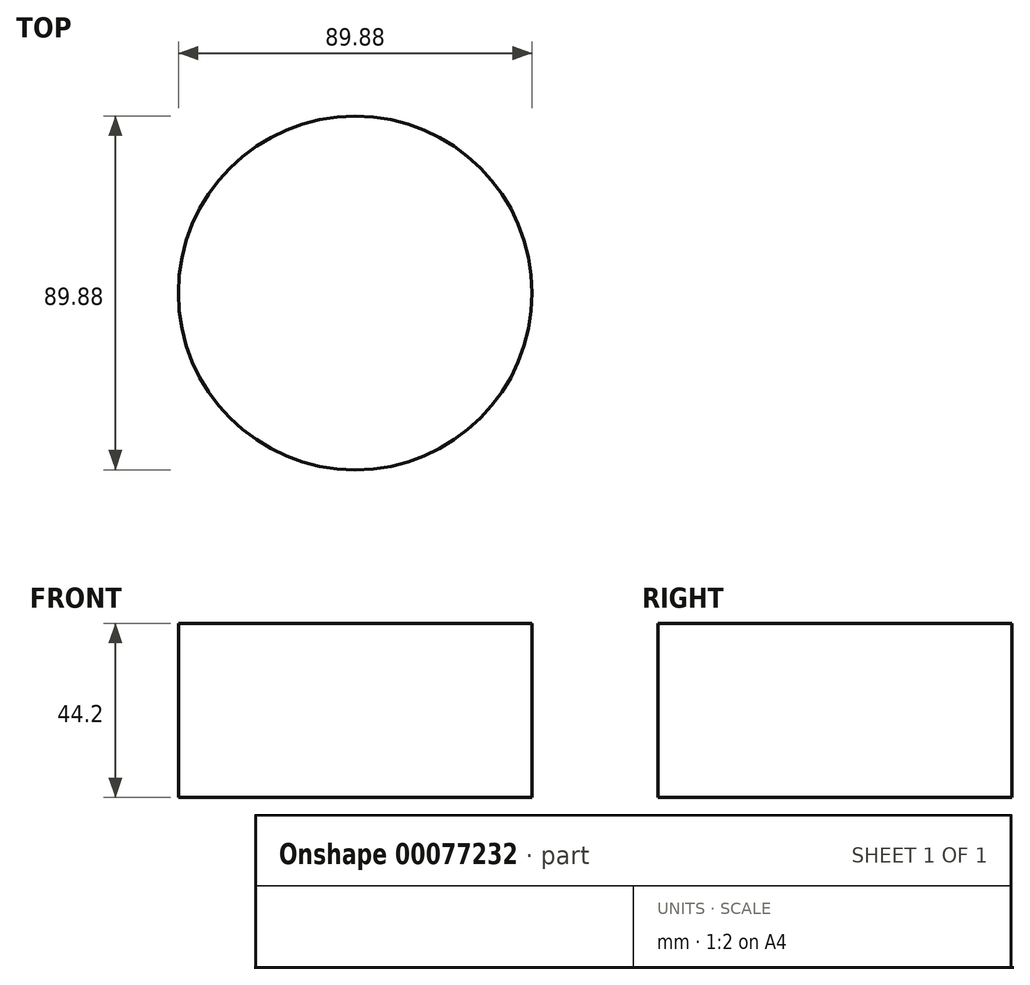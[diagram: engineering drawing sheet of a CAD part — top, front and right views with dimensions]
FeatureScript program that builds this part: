
annotation { "Feature Type Name" : "Feature", "Feature Type Description" : "" }
export const myFeature = defineFeature(function(context is Context, id is Id, definition is map)
    precondition{}
    {
        {
            var Q0;
            Q0=qCreatedBy(makeId("Front.planeOp"),FACE);
            var sketch = newSketch(context, id + "F0", { "sketchPlane" : qUnion([Q0])});
            skArc(sketch, "E0", {"start": v(-83.08, -5.99) * mm, "mid": v(-39.18, -35.68) * mm, "end": v(0, 0) * mm});
            skArc(sketch, "E1", {"start": v(3.36, 7.06) * mm, "mid": v(-42.66, 19.09) * mm, "end": v(-83.08, -5.99) * mm});
            skSolve(sketch);
        }
        {
            var Q0;
            Q0=qCreatedBy(makeId("Top.planeOp"),FACE);
            var sketch = newSketch(context, id + "F1", { "sketchPlane" : qUnion([Q0])});
            skCircle(sketch, "E2", {"center": v(0, 0) * mm, "radius": 44.94 * mm});
            skSolve(sketch);
        }
        {
            var Q0;
            Q0=makeQuery(id+"F1.imprint","IMPRINT",FACE,{"disambiguationData":[TD([[makeQuery(id+"F1.imprint","IMPRINT",EDGE,{"derivedFrom":sQuery(id+"F1.wireOp",EDGE,"E2")}),1.0]])]});
            extrude(context, id + "F2", {"entities" : qUnion([Q0]), "depth" : 44.2 * mm});
        }
    });
